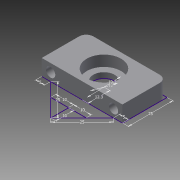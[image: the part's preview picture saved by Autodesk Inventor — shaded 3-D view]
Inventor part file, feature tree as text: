
AUTODESK INVENTOR PART (.ipt)
format: ipt  version: 2015 (Build 190159000, 159)  size: 122,880 bytes
history: native  units: in
note: dims shown in document units (in); Inventor stores cm internally (conversion verified against a paired STEP export)
features: extrude x3, sketch x2, fillet x1
ambient origin geometry x8: Origin, YZ Plane, XZ Plane, XY Plane, X Axis, Y Axis, Z Axis, Center Point
bodies: Solid1 (feature_tree)
feature tree (6):
  sketch  "Sketch1"  dims[d0=0.3937in d1=0.3937in]
  extrude  "Extrusion1"  Depth=0.3937in
  extrude  "Extrusion2"  Depth=0.1575in
  extrude  "Extrusion3"  Depth=0.1575in
  fillet  "Fillet1"  Radius=0.4843in
  sketch  "Sketch2"  dims[d2=0.3937in d3=0.9843in d4=0.9843in d5=0.4843in d6=0.7598in d7=0.4724in d8=0.1969in d9=0.1969in d10=0.9843in d11=0.1181in d12=0.0in d13=0.3543in d14=0.0in d15=0.1969in d16=0.1969in d17=0.2047in d18=0.2047in d19=1.0236in d20=0.0in d21=0.1575in]
